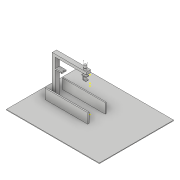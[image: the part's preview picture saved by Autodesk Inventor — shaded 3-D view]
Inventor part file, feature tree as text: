
AUTODESK INVENTOR PART (.ipt)
format: ipt  version: 2019 (Build 230136000, 136)  size: 229,888 bytes
history: native  units: in
note: dims shown in document units (in); Inventor stores cm internally (conversion verified against a paired STEP export)
features: sketch x28, extrude x19
ambient origin geometry x8: Origin, YZ Plane, XZ Plane, XY Plane, X Axis, Y Axis, Z Axis, Center Point
bodies: Solid1 (feature_tree)
feature tree (47):
  extrude  "Extrusion1"  Depth=23.622in
  extrude  "Extrusion2"  Depth=3.937in
  extrude  "Extrusion3"  Depth=1.378in
  extrude  "Extrusion4"  Depth=2.7559in
  sketch  "Sketch5"  dims[d10=2.7559in d11=7.874in]
  extrude  "Extrusion5"  Depth=7.874in
  sketch  "Sketch7"  dims[d16=0.3937in d17=0.3937in d18=0.0in]
  extrude  "Extrusion6"  Depth=0.3937in TaperAngle=0.0deg
  extrude  "Extrusion7"  Depth=0.3937in TaperAngle=0.0deg
  extrude  "Extrusion8"  Depth=9.8425in TaperAngle=0.0deg
  extrude  "Extrusion9"  Depth=0.7874in TaperAngle=0.0deg
  sketch  "Sketch12"  dims[d37=1.1811in d38=0.0in d39=1.1811in d40=0.0in]
  sketch  "Sketch13"  dims[d41=0.7874in d42=0.0in d43=0.7874in d44=0.0in]
  extrude  "Extrusion10"  Depth=2.7559in TaperAngle=0.0deg
  extrude  "Extrusion11"  Depth=1.9685in TaperAngle=0.0deg
  extrude  "Extrusion12"  Depth=1.1811in TaperAngle=0.0deg
  extrude  "Extrusion13"  Depth=0.7874in TaperAngle=0.0deg
  extrude  "Extrusion14"  Depth=2.5591in
  extrude  "Extrusion15"  Depth=2.5591in
  extrude  "Extrusion16"  [1 undecoded]
  extrude  "Extrusion17"  [1 undecoded]
  extrude  "Extrusion18"  [1 undecoded]
  sketch  "Sketch23"
  sketch  "Sketch24"
  sketch  "Sketch25"
  extrude  "Extrusion19"  [1 undecoded]
  sketch  "Sketch27"
  sketch  "Sketch28"
  sketch  "Sketch1"  dims[d0=29.5276in d1=23.622in]
  sketch  "Sketch2"  dims[d2=0.1969in d3=0.0in d4=3.937in]
  sketch  "Sketch3"  dims[d5=0.9843in d6=1.378in]
  sketch  "Sketch4"  dims[d7=11.811in d8=0.0in d9=2.7559in]
  sketch  "Sketch6"  dims[d12=1.9685in d13=0.0in d14=0.3937in d15=0.0in]
  sketch  "Sketch8"  dims[d19=0.3937in d20=0.0in d21=9.8425in d22=0.0in]
  sketch  "Sketch9"  dims[d23=0.3937in d24=0.0in d25=0.7874in d26=0.0in]
  sketch  "Sketch10"  dims[d27=2.3622in d28=0.0in d29=2.7559in d30=0.0in]
  sketch  "Sketch11"  dims[d31=0.1969in d32=0.0in d33=1.9685in d34=3.5433in d35=0.0in d36=0.0in]
  sketch  "Sketch14"  dims[d45=0.1969in d46=0.0in d47=2.5591in]
  sketch  "Sketch15"  dims[d48=1.5748in d49=2.5591in]
  sketch  "Sketch16"  dims[d50=3.1496in d51=0.0in]
  sketch  "Sketch17"
  sketch  "Sketch18"
  sketch  "Sketch19"
  sketch  "Sketch20"
  sketch  "Sketch21"
  sketch  "Sketch22"
  sketch  "Sketch26"
note: 4 required parameter values undecoded (feature->parameter linkage not recoverable at this tier; creation-order binding heuristic only, values carry confidence <= 0.55)
